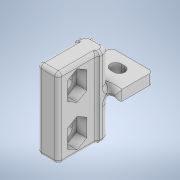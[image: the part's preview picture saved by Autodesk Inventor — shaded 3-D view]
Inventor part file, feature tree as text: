
AUTODESK INVENTOR PART (.ipt)
format: ipt  version: 2021 (Build 250183000, 183)  size: 449,024 bytes
history: native  units: mm
features: extrude x6, sketch x6, fillet x2, projected_geometry x2
ambient origin geometry x8: Origin, YZ Plane, XZ Plane, XY Plane, X Axis, Y Axis, Z Axis, Center Point
bodies: Solid1 (feature_tree)
feature tree (16):
  extrude  "Extrusion1"  Depth=10.0mm
  extrude  "Extrusion2"  Depth=7.0mm
  extrude  "Extrusion3"  Depth=10.0mm
  extrude  "Extrusion6"  Depth=6.0mm
  extrude  "Extrusion7"  Depth=5.8mm
  extrude  "Extrusion8"  Depth=1.0mm
  fillet  "Fillet3"  Radius=10.0mm
  fillet  "Fillet4"  Radius=5.5mm
  sketch  "Sketch1"  dims[d0=12.0mm d1=10.0mm]
  sketch  "Sketch2"  dims[d2=3.0mm d3=0.0mm d4=7.0mm]
  sketch  "Sketch3"  dims[d5=23.0mm d6=10.0mm]
  sketch  "Sketch7"  dims[d7=3.0mm d8=0.0mm d9=6.0mm]
  sketch  "Sketch8"  dims[d10=11.5mm d11=0.0mm d37=5.8mm]
  projected_geometry  "Projected Loop2"
  sketch  "Sketch9"  dims[d38=3.2mm d39=1.0mm d40=10.0mm d41=0.0mm d43=5.5mm d44=12.0mm d45=5.5mm d46=1.0mm d47=3.2mm d48=1.0mm d49=3.2mm d50=3.0mm d51=0.0mm d52=5.6mm d53=5.6mm d54=5.6mm d55=5.6mm d56=3.0mm d57=0.0mm d58=1.0mm d59=2.2mm]
  projected_geometry  "Projected Loop3"
